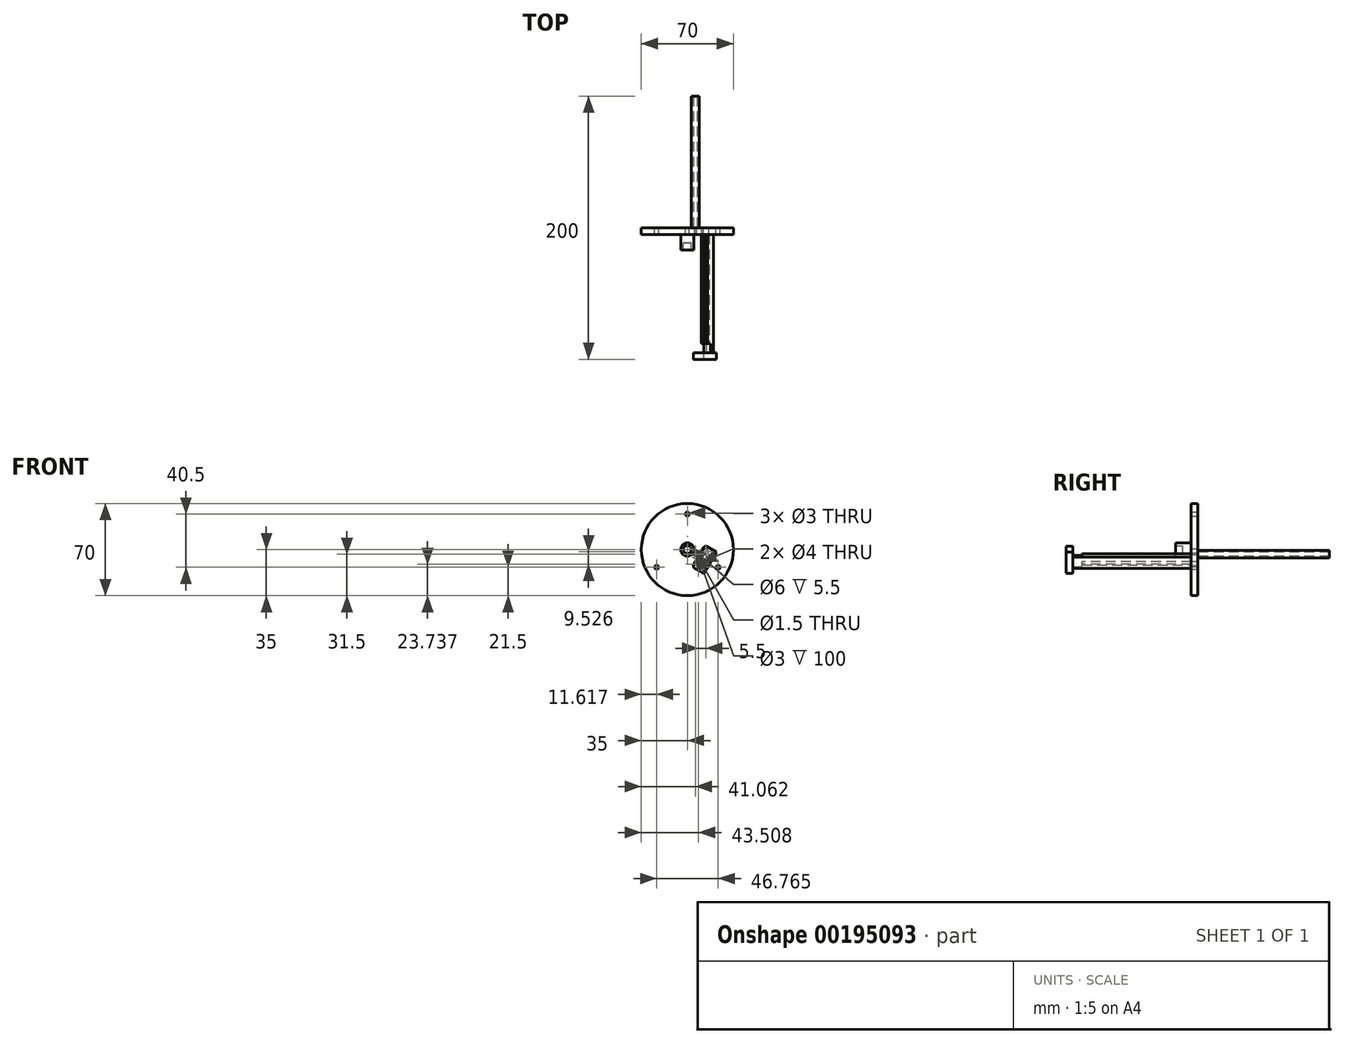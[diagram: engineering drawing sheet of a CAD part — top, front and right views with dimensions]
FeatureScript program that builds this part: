
annotation { "Feature Type Name" : "Feature", "Feature Type Description" : "" }
export const myFeature = defineFeature(function(context is Context, id is Id, definition is map)
    precondition{}
    {
        {
            var Q0;
            Q0=qCreatedBy(makeId("Front.planeOp"),FACE);
            var sketch = newSketch(context, id + "F0", { "sketchPlane" : qUnion([Q0])});
            skCircle(sketch, "E0", {"center": v(0, 0) * mm, "radius": 35 * mm});
            skSolve(sketch);
        }
        {
            var Q0;
            Q0 = qSketchRegion(id + "F0", true);
            extrude(context, id + "F1", {"entities" : qUnion([Q0]), "depth" : 5 * mm});
        }
        {
            var Q0;
            Q0=makeQuery(id+"F1.opExtrude","CAP_FACE",FACE,{"disambiguationData":[OSD([sQuery(id+"F0.wireOp",EDGE,"E0")])],"isStart":false});
            var sketch = newSketch(context, id + "F2", { "sketchPlane" : qUnion([Q0])});
            skCircle(sketch, "E1", {"center": v(0, 0) * mm, "radius": 3 * mm});
            skCircle(sketch, "E2", {"center": v(0, 0) * mm, "radius": 5 * mm});
            skSolve(sketch);
        }
        {
            var Q0;
            Q0 = qSketchRegion(id + "F2", true);
            extrude(context, id + "F3", {"entities" : qUnion([Q0]), "operationType" : NewBodyOperationType.ADD, "depth" : 12 * mm});
        }
        {
            var Q0;
            {var subQ0=sQuery(id+"F0.wireOp",EDGE,"E0");Q0=makeQuery(id+"F3.boolean.opBoolean","SPLIT",FACE,{"disambiguationData":[TD([makeQuery(id+"F1.opExtrude","SWEPT_FACE",FACE,{"disambiguationData":[OSD([subQ0])]})])],"derivedFrom":makeQuery(id+"F1.opExtrude","CAP_FACE",FACE,{"disambiguationData":[OSD([subQ0])],"isStart":false})});}
            var sketch = newSketch(context, id + "F4", { "sketchPlane" : qUnion([Q0])});
            skLineSegment(sketch, "E3", {"start": v(0, 0) * mm, "end": v(0, 24.21) * mm, "construction": true});
            skLineSegment(sketch, "E4", {"start": v(0, 0) * mm, "end": v(39.64, -22.89) * mm, "construction": true});
            skLineSegment(sketch, "E5", {"start": v(19.82, -5.67) * mm, "end": v(14.82, -14.33) * mm});
            skPoint(sketch, "E5.startSnap0", {"position": v(19.82, -11.44) * mm});
            skLineSegment(sketch, "E6", {"start": v(14.82, -14.33) * mm, "end": v(10.5, -11.83) * mm});
            skLineSegment(sketch, "E7", {"start": v(10.5, -11.83) * mm, "end": v(15.5, -3.17) * mm});
            skLineSegment(sketch, "E8", {"start": v(15.5, -3.17) * mm, "end": v(19.82, -5.67) * mm});
            skSolve(sketch);
        }
        {
            var Q0;
            Q0 = qSketchRegion(id + "F4", true);
            extrude(context, id + "F5", {"entities" : qUnion([Q0]), "operationType" : NewBodyOperationType.ADD, "depth" : 83 * mm});
        }
        {
            var Q0;
            Q0=makeQuery(id+"F1.opExtrude","CAP_FACE",FACE,{"disambiguationData":[OSD([sQuery(id+"F0.wireOp",EDGE,"E0")])],"isStart":true});
            var sketch = newSketch(context, id + "F6", { "sketchPlane" : qUnion([Q0])});
            skLineSegment(sketch, "E9", {"start": v(0, 0) * mm, "end": v(0, 44.5) * mm, "construction": true});
            skLineSegment(sketch, "E10", {"start": v(0, 0) * mm, "end": v(44.04, -25.43) * mm, "construction": true});
            skLineSegment(sketch, "E11", {"start": v(0, 0) * mm, "end": v(-56.95, -32.88) * mm, "construction": true});
            skCircle(sketch, "E12", {"center": v(0, 0) * mm, "radius": 27 * mm, "construction": true});
            skPoint(sketch, "E13", {"position": v(0, 27) * mm});
            skPoint(sketch, "E14", {"position": v(-23.38, -13.5) * mm});
            skPoint(sketch, "E15", {"position": v(23.38, -13.5) * mm});
            skSolve(sketch);
        }
        {
            var Q0;
            Q0=sQuery(id+"F6.wireOp",VERTEX,"E13");
            var Q1;
            Q1=sQuery(id+"F6.wireOp",VERTEX,"E14");
            var Q2;
            Q2=sQuery(id+"F6.wireOp",VERTEX,"E15");
            var Q3;
            Q3=makeQuery(id+"F1.opExtrude","SWEPT_BODY",BODY,{"disambiguationData":[OSD([sQuery(id+"F0.wireOp",EDGE,"E0")])]});
            hole(context, id + "F7", {"style" : HoleStyle.SIMPLE, "endStyle" : HoleEndStyle.BLIND, "standardTappedOrClearance" : lookupTablePath({ "standard" : "ISO", "size" : "3", "type" : "Drilled" }), "standardBlindInLast" : lookupTablePath({ "standard" : "ISO", "size" : "3", "type" : "Drilled" }), "holeDiameter" : 3 * mm, "holeDepth" : 6 * mm, "locations" : qUnion([Q0, Q1, Q2]), "scope" : qUnion([Q3])});
        }
        {
            var Q0;
            Q0=makeQuery(id+"F5.opExtrude","CAP_FACE",FACE,{"disambiguationData":[OSD([sQuery(id+"F4.wireOp",EDGE,"E5"),sQuery(id+"F4.wireOp",EDGE,"E6"),sQuery(id+"F4.wireOp",EDGE,"E7"),sQuery(id+"F4.wireOp",EDGE,"E8")])],"isStart":false});
            var sketch = newSketch(context, id + "F8", { "sketchPlane" : qUnion([Q0])});
            skLineSegment(sketch, "E16", {"start": v(12, -9.23) * mm, "end": v(13, -10.98) * mm});
            skLineSegment(sketch, "E17", {"start": v(13.87, -10.98) * mm, "end": v(16.44, -6.52) * mm});
            skLineSegment(sketch, "E18", {"start": v(16.01, -5.77) * mm, "end": v(14, -5.77) * mm});
            skLineSegment(sketch, "E19", {"start": v(14, -5.77) * mm, "end": v(12, -9.23) * mm});
            skPoint(sketch, "E20.visualSharp", {"position": v(16.88, -5.77) * mm});
            skArc(sketch, "E20.filletArc", {"start": v(16.44, -6.52) * mm, "mid": v(16.44, -6.02) * mm, "end": v(16.01, -5.77) * mm});
            skPoint(sketch, "E21.visualSharp", {"position": v(13.43, -11.73) * mm});
            skArc(sketch, "E21.filletArc", {"start": v(13, -10.98) * mm, "mid": v(13.43, -11.23) * mm, "end": v(13.87, -10.98) * mm});
            skSolve(sketch);
        }
        {
            var Q0;
            Q0 = qSketchRegion(id + "F8", true);
            var Q1;
            {var subQ0=sQuery(id+"F0.wireOp",EDGE,"E0");Q1=makeQuery(id+"F3.boolean.opBoolean","SPLIT",FACE,{"disambiguationData":[TD([makeQuery(id+"F1.opExtrude","SWEPT_FACE",FACE,{"disambiguationData":[OSD([subQ0])]})])],"derivedFrom":makeQuery(id+"F1.opExtrude","CAP_FACE",FACE,{"disambiguationData":[OSD([subQ0])],"isStart":false})});}
            extrude(context, id + "F9", {"entities" : qUnion([Q0]), "operationType" : NewBodyOperationType.REMOVE, "endBound" : BoundingType.UP_TO_SURFACE, "oppositeDirection" : true, "endBoundEntityFace" : qUnion([Q1]), "depth" : 25 * mm});
        }
        {
            var Q0;
            Q0=makeQuery(id+"F3.boolean.opBoolean","SPLIT",FACE,{"disambiguationData":[TD([makeQuery(id+"F3.opExtrude","SWEPT_FACE",FACE,{"disambiguationData":[OSD([sQuery(id+"F2.wireOp",EDGE,"E1")])]})])],"derivedFrom":makeQuery(id+"F1.opExtrude","CAP_FACE",FACE,{"disambiguationData":[OSD([sQuery(id+"F0.wireOp",EDGE,"E0")])],"isStart":false})});
            var sketch = newSketch(context, id + "F10", { "sketchPlane" : qUnion([Q0])});
            skCircle(sketch, "E22.0", {"center": v(0, 0) * mm, "radius": 3 * mm});
            skSolve(sketch);
        }
        {
            var Q0;
            Q0 = qSketchRegion(id + "F10", true);
            extrude(context, id + "F11", {"entities" : qUnion([Q0]), "operationType" : NewBodyOperationType.ADD, "depth" : 6.5 * mm});
        }
        {
            var Q0;
            Q0=makeQuery(id+"F5.opExtrude","CAP_FACE",FACE,{"disambiguationData":[OSD([sQuery(id+"F4.wireOp",EDGE,"E5"),sQuery(id+"F4.wireOp",EDGE,"E6"),sQuery(id+"F4.wireOp",EDGE,"E7"),sQuery(id+"F4.wireOp",EDGE,"E8")])],"isStart":false});
            var sketch = newSketch(context, id + "F12", { "sketchPlane" : qUnion([Q0])});
            skLineSegment(sketch, "E23", {"start": v(14.82, -14.33) * mm, "end": v(19.82, -5.67) * mm});
            skLineSegment(sketch, "E24", {"start": v(19.82, -5.67) * mm, "end": v(17.66, -4.42) * mm});
            skLineSegment(sketch, "E25", {"start": v(17.66, -4.42) * mm, "end": v(12.66, -13.08) * mm});
            skLineSegment(sketch, "E26", {"start": v(12.66, -13.08) * mm, "end": v(14.82, -14.33) * mm});
            skPoint(sketch, "E27.visualSharp", {"position": v(17.66, -4.42) * mm});
            skLineSegment(sketch, "E27.filletArc", {"start": v(17.66, -4.42) * mm, "end": v(17.66, -4.42) * mm});
            skPoint(sketch, "E28.visualSharp", {"position": v(12.66, -13.08) * mm});
            skLineSegment(sketch, "E28.filletArc", {"start": v(12.66, -13.08) * mm, "end": v(12.66, -13.08) * mm});
            skSolve(sketch);
        }
        {
            var Q0;
            Q0 = qSketchRegion(id + "F12", true);
            extrude(context, id + "F13", {"entities" : qUnion([Q0]), "operationType" : NewBodyOperationType.ADD, "depth" : 7 * mm});
        }
        {
            var Q0;
            Q0=makeQuery(id+"F13.opExtrude","CAP_FACE",FACE,{"disambiguationData":[OSD([sQuery(id+"F12.wireOp",EDGE,"E23"),sQuery(id+"F12.wireOp",EDGE,"E24"),sQuery(id+"F12.wireOp",EDGE,"E25"),sQuery(id+"F12.wireOp",EDGE,"E26")])],"isStart":false});
            var sketch = newSketch(context, id + "F14", { "sketchPlane" : qUnion([Q0])});
            skLineSegment(sketch, "E29", {"start": v(12.57, -18.23) * mm, "end": v(5.64, -14.23) * mm});
            skLineSegment(sketch, "E30", {"start": v(4.91, -11.5) * mm, "end": v(12.41, 1.5) * mm});
            skLineSegment(sketch, "E31", {"start": v(15.14, 2.23) * mm, "end": v(22.07, -1.77) * mm});
            skPoint(sketch, "E32.visualSharp", {"position": v(13.41, 3.23) * mm});
            skArc(sketch, "E32.filletArc", {"start": v(15.14, 2.23) * mm, "mid": v(13.62, 2.43) * mm, "end": v(12.41, 1.5) * mm});
            skPoint(sketch, "E33.visualSharp", {"position": v(3.91, -13.23) * mm});
            skArc(sketch, "E33.filletArc", {"start": v(4.91, -11.5) * mm, "mid": v(4.71, -13.01) * mm, "end": v(5.64, -14.23) * mm});
            skLineSegment(sketch, "E34", {"start": v(17.32, -10) * mm, "end": v(12.64, -7.3) * mm, "construction": true});
            skLineSegment(sketch, "E35", {"start": v(12.57, -18.23) * mm, "end": v(22.07, -1.77) * mm});
            skLineSegment(sketch, "E36", {"start": v(17.32, -10) * mm, "end": v(25.37, 3.94) * mm, "construction": true});
            skSolve(sketch);
        }
        {
            var Q0;
            Q0=makeQuery(id+"F14.imprint","IMPRINT",FACE,{"disambiguationData":[TD([[makeQuery(id+"F14.imprint","IMPRINT",EDGE,{"derivedFrom":sQuery(id+"F14.wireOp",EDGE,"E30")}),-1.0]])]});
            var Q1;
            {var subQ0=sQuery(id+"F14.wireOp",EDGE,"nDAFDezV-Gyml-wG9m-Qvhd-3wH3xEkhHGa3");Q1=makeQuery(id+"F14.imprint","IMPRINT",FACE,{"disambiguationData":[TD([[makeQuery(id+"F14.imprint","IMPRINT",EDGE,{"derivedFrom":subQ0}),-1.0]])]});}
            var Q2;
            {var subQ1=makeQuery(id+"F13.opExtrude","CAP_EDGE",EDGE,{"disambiguationData":[OSD([sQuery(id+"F12.wireOp",EDGE,"E24")])],"isStart":false});Q2=makeQuery(id+"F14.imprint","IMPRINT",FACE,{"disambiguationData":[TD([[makeQuery(id+"F14.imprint","IMPRINT",EDGE,{"derivedFrom":subQ1}),-1.0]])]});}
            extrude(context, id + "F15", {"entities" : qUnion([Q0, Q1, Q2]), "depth" : 5 * mm});
        }
        {
            var Q0;
            Q0=makeQuery(id+"F15.opExtrude","CAP_FACE",FACE,{"disambiguationData":[OSD([sQuery(id+"F14.wireOp",EDGE,"E29"),sQuery(id+"F14.wireOp",EDGE,"E30"),sQuery(id+"F14.wireOp",EDGE,"E31"),sQuery(id+"F14.wireOp",EDGE,"E32.filletArc"),sQuery(id+"F14.wireOp",EDGE,"E33.filletArc"),sQuery(id+"F14.wireOp",EDGE,"E35")])],"isStart":false});
            var sketch = newSketch(context, id + "F16", { "sketchPlane" : qUnion([Q0])});
            skLineSegment(sketch, "E37", {"start": v(0, 0) * mm, "end": v(40.73, -23.51) * mm, "construction": true});
            skPoint(sketch, "E38", {"position": v(8.5, -11.26) * mm});
            skPoint(sketch, "E39", {"position": v(14, -1.74) * mm});
            skLineSegment(sketch, "E40", {"start": v(0, 0) * mm, "end": v(13.9, 24.07) * mm, "construction": true});
            skSolve(sketch);
        }
        {
            var Q0;
            Q0=sQuery(id+"F16.wireOp",VERTEX,"E39");
            var Q1;
            Q1=sQuery(id+"F16.wireOp",VERTEX,"E38");
            var Q2;
            Q2=makeQuery(id+"F1.opExtrude","SWEPT_BODY",BODY,{"disambiguationData":[OSD([sQuery(id+"F0.wireOp",EDGE,"E0")])]});
            hole(context, id + "F17", {"style" : HoleStyle.SIMPLE, "endStyle" : HoleEndStyle.BLIND, "standardTappedOrClearance" : lookupTablePath({ "standard" : "ISO", "size" : "4", "type" : "Drilled" }), "standardBlindInLast" : lookupTablePath({ "standard" : "ISO", "size" : "4", "type" : "Drilled" }), "holeDiameter" : 4 * mm, "holeDepth" : 10 * mm, "locations" : qUnion([Q0, Q1]), "scope" : qUnion([Q2])});
        }
        {
            var Q0;
            {var subQ0=sQuery(id+"F0.wireOp",EDGE,"E0");Q0=makeQuery(id+"F9.boolean.opBoolean","MERGE",FACE,{"derivedFrom":[makeQuery(id+"F3.boolean.opBoolean","SPLIT",FACE,{"disambiguationData":[TD([makeQuery(id+"F1.opExtrude","SWEPT_FACE",FACE,{"disambiguationData":[OSD([subQ0])]})])],"derivedFrom":makeQuery(id+"F1.opExtrude","CAP_FACE",FACE,{"disambiguationData":[OSD([subQ0])],"isStart":false})}),makeQuery(id+"F9.opExtrude","CAP_FACE",FACE,{"disambiguationData":[OSD([sQuery(id+"F8.wireOp",EDGE,"E16"),sQuery(id+"F8.wireOp",EDGE,"E17"),sQuery(id+"F8.wireOp",EDGE,"E18"),sQuery(id+"F8.wireOp",EDGE,"E19"),sQuery(id+"F8.wireOp",EDGE,"E20.filletArc"),sQuery(id+"F8.wireOp",EDGE,"E21.filletArc")])],"isStart":false})]});}
            var sketch = newSketch(context, id + "F18", { "sketchPlane" : qUnion([Q0])});
            skLineSegment(sketch, "E41", {"start": v(0, 0) * mm, "end": v(12.12, -7) * mm, "construction": true});
            skPoint(sketch, "E42", {"position": v(6.06, -3.5) * mm});
            skSolve(sketch);
        }
        {
            var Q0;
            Q0=sQuery(id+"F18.wireOp",VERTEX,"E42");
            var Q1;
            Q1=makeQuery(id+"F1.opExtrude","SWEPT_BODY",BODY,{"disambiguationData":[OSD([sQuery(id+"F0.wireOp",EDGE,"E0")])]});
            hole(context, id + "F19", {"style" : HoleStyle.SIMPLE, "endStyle" : HoleEndStyle.BLIND, "standardTappedOrClearance" : lookupTablePath({ "standard" : "ISO", "size" : "1.5", "type" : "Drilled" }), "standardBlindInLast" : lookupTablePath({ "standard" : "ISO", "size" : "1.5", "type" : "Drilled" }), "holeDiameter" : 1.5 * mm, "holeDepth" : 10 * mm, "locations" : qUnion([Q0]), "scope" : qUnion([Q1])});
        }
        {
            var Q0;
            Q0=makeQuery(id+"F1.opExtrude","CAP_FACE",FACE,{"disambiguationData":[OSD([sQuery(id+"F0.wireOp",EDGE,"E0")])],"isStart":true});
            var sketch = newSketch(context, id + "F20", { "sketchPlane" : qUnion([Q0])});
            skCircle(sketch, "E43", {"center": v(-6.06, -3.5) * mm, "radius": 1.5 * mm});
            skCircle(sketch, "E44", {"center": v(-6.06, -3.5) * mm, "radius": 3 * mm});
            skSolve(sketch);
        }
        {
            var Q0;
            Q0=makeQuery(id+"F20.imprint","IMPRINT",FACE,{"disambiguationData":[TD([[makeQuery(id+"F20.imprint","IMPRINT",EDGE,{"derivedFrom":sQuery(id+"F20.wireOp",EDGE,"E43")}),-1.0]])]});
            extrude(context, id + "F21", {"entities" : qUnion([Q0]), "operationType" : NewBodyOperationType.ADD, "depth" : 100 * mm});
        }
    });
